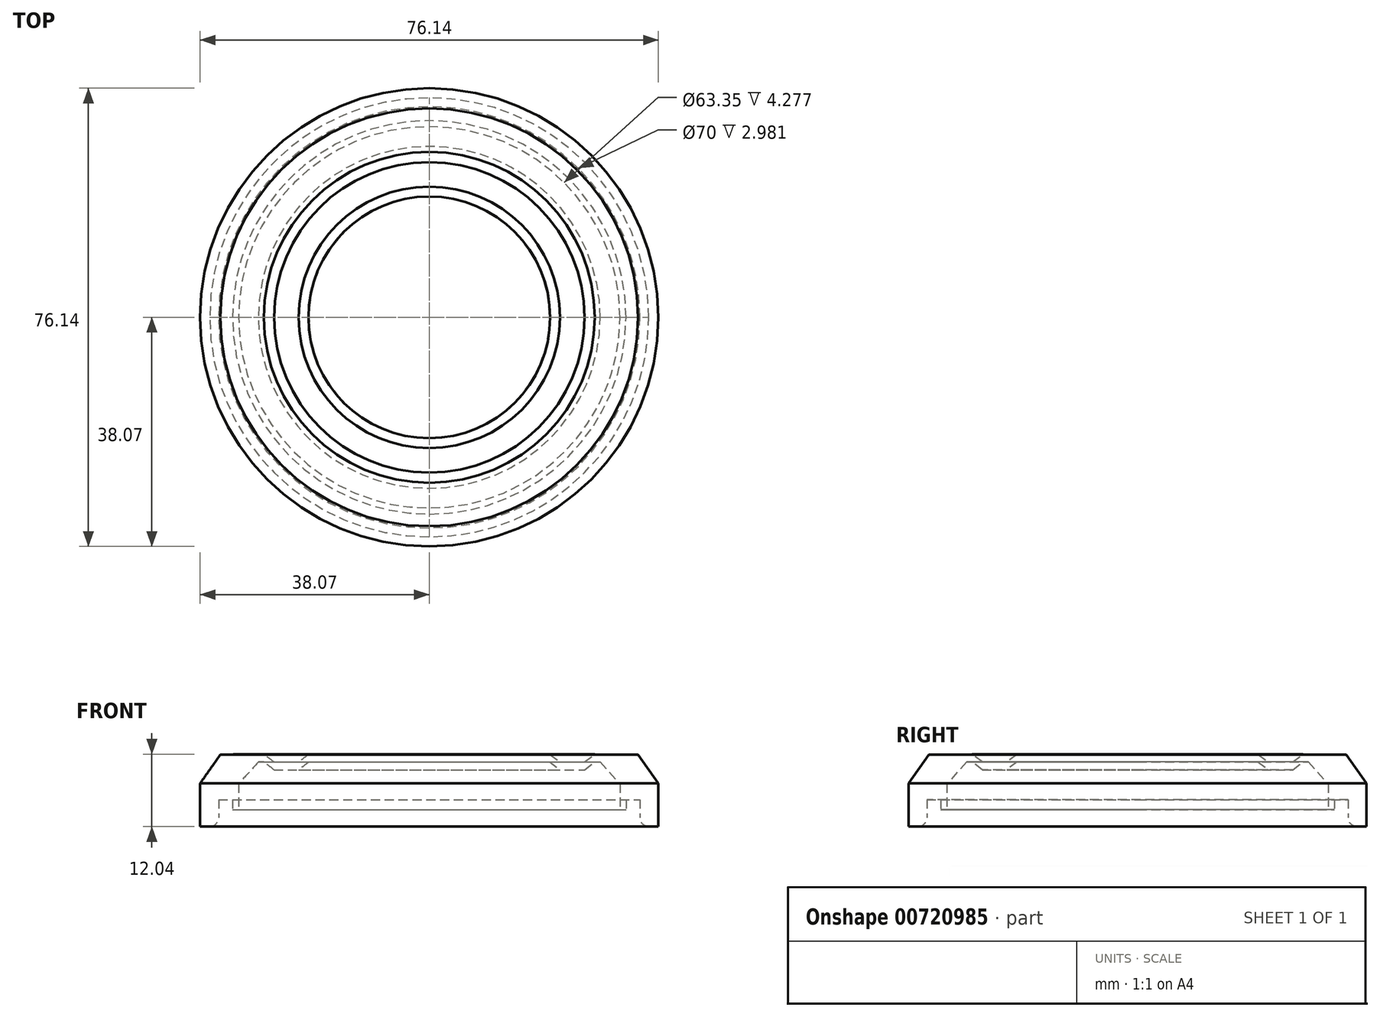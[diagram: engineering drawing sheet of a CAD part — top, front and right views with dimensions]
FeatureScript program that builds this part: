
annotation { "Feature Type Name" : "Feature", "Feature Type Description" : "" }
export const myFeature = defineFeature(function(context is Context, id is Id, definition is map)
    precondition{}
    {
        {
            var Q0;
            Q0=qCreatedBy(makeId("Front.planeOp"),FACE);
            var sketch = newSketch(context, id + "F0", { "sketchPlane" : qUnion([Q0])});
            skLineSegment(sketch, "E0", {"start": v(0, 0) * mm, "end": v(0, 19.91) * mm});
            skPoint(sketch, "E1.visualSharp", {"position": v(31, 6) * mm});
            skPoint(sketch, "E2.visualSharp", {"position": v(38, 6) * mm});
            skPoint(sketch, "E3.visualSharp", {"position": v(39, 6.04) * mm});
            skPoint(sketch, "E4.visualSharp", {"position": v(44, 6.04) * mm});
            skPoint(sketch, "E5.visualSharp", {"position": v(44.9, 6.04) * mm});
            skPoint(sketch, "E6.visualSharp", {"position": v(49.9, 6.04) * mm});
            skPoint(sketch, "E7.visualSharp", {"position": v(49.9, 0.04) * mm});
            skPoint(sketch, "E8.visualSharp", {"position": v(38, 0) * mm});
            skPoint(sketch, "E9.visualSharp", {"position": v(39, 0.01) * mm});
            skPoint(sketch, "E10.visualSharp", {"position": v(44, 0.01) * mm});
            skPoint(sketch, "E11.visualSharp", {"position": v(44.9, 0.04) * mm});
            skLineSegment(sketch, "E12", {"start": v(35, 8.36) * mm, "end": v(35, 11) * mm});
            skLineSegment(sketch, "E13", {"start": v(33.01, 11.34) * mm, "end": v(35, 11.34) * mm});
            skLineSegment(sketch, "E14", {"start": v(35, 11.34) * mm, "end": v(35, 8.36) * mm});
            skLineSegment(sketch, "E15", {"start": v(36.47, 6.86) * mm, "end": v(38.07, 6.86) * mm});
            skLineSegment(sketch, "E16", {"start": v(38.07, 6.86) * mm, "end": v(38.07, 14.07) * mm});
            skLineSegment(sketch, "E17", {"start": v(38.07, 14.07) * mm, "end": v(34.7, 18.84) * mm});
            skLineSegment(sketch, "E18", {"start": v(0, 18.84) * mm, "end": v(0, 17.6) * mm});
            skLineSegment(sketch, "E19", {"start": v(0, 17.6) * mm, "end": v(20, 17.6) * mm});
            skLineSegment(sketch, "E20", {"start": v(32.32, 9.7) * mm, "end": v(32.69, 9.7) * mm});
            skPoint(sketch, "E21.orphan", {"position": v(33, 6) * mm});
            skLineSegment(sketch, "E22", {"start": v(33.01, 11.34) * mm, "end": v(32.69, 11.34) * mm});
            skLineSegment(sketch, "E23", {"start": v(32.69, 11.34) * mm, "end": v(32.69, 9.7) * mm});
            skLineSegment(sketch, "E24", {"start": v(32.69, 9.7) * mm, "end": v(31.67, 9.7) * mm});
            skLineSegment(sketch, "E25", {"start": v(31.67, 9.7) * mm, "end": v(31.67, 13.98) * mm});
            skLineSegment(sketch, "E26", {"start": v(31.67, 13.98) * mm, "end": v(28.4, 17.6) * mm});
            skPoint(sketch, "E27.start.orphan", {"position": v(32.32, 14.07) * mm});
            skPoint(sketch, "E28.start.orphan", {"position": v(33.01, 11.02) * mm});
            skPoint(sketch, "E29.orphan", {"position": v(33.01, 9.7) * mm});
            skPoint(sketch, "E30.endSnap0", {"position": v(17.35, 18.84) * mm});
            skLineSegment(sketch, "E31.trimOffspring", {"start": v(20.08, 18.84) * mm, "end": v(0, 18.84) * mm});
            skPoint(sketch, "E32.start.orphan", {"position": v(27.48, 17.6) * mm});
            skPoint(sketch, "E33.end.orphan", {"position": v(27.48, 18.9) * mm});
            skLineSegment(sketch, "E34", {"start": v(34.7, 18.84) * mm, "end": v(27.48, 18.9) * mm});
            skLineSegment(sketch, "E35", {"start": v(28.4, 17.6) * mm, "end": v(27.48, 17.6) * mm});
            skLineSegment(sketch, "E36", {"start": v(27.48, 18.9) * mm, "end": v(25.8, 17.6) * mm});
            skLineSegment(sketch, "E37", {"start": v(20.08, 18.84) * mm, "end": v(21.71, 17.6) * mm});
            skLineSegment(sketch, "E38", {"start": v(21.71, 17.6) * mm, "end": v(25.8, 17.6) * mm});
            skLineSegment(sketch, "E39", {"start": v(27.48, 17.6) * mm, "end": v(25.8, 16.3) * mm});
            skLineSegment(sketch, "E40", {"start": v(25.8, 16.3) * mm, "end": v(21.7, 16.3) * mm});
            skLineSegment(sketch, "E41", {"start": v(21.7, 16.3) * mm, "end": v(20, 17.6) * mm});
            skPoint(sketch, "E42.orphan", {"position": v(17.35, 17.6) * mm});
            skLineSegment(sketch, "E43", {"start": v(40.5, 0.01) * mm, "end": v(40.4, 0.01) * mm});
            skLineSegment(sketch, "E44", {"start": v(36.1, 6) * mm, "end": v(36.4, 6) * mm});
            skLineSegment(sketch, "E45", {"start": v(33, 6) * mm, "end": v(32.9, 6) * mm});
            skLineSegment(sketch, "E46", {"start": v(36.4, 6) * mm, "end": v(36.1, 6) * mm});
            skLineSegment(sketch, "E47", {"start": v(39, 4.13) * mm, "end": v(39, 1.43) * mm});
            skPoint(sketch, "E48.visualSharp", {"position": v(34.64, 11.02) * mm});
            skLineSegment(sketch, "E49.filletArc", {"start": v(33.01, 11.02) * mm, "end": v(33.01, 11.02) * mm});
            skArc(sketch, "E50", {"start": v(35, 8.37) * mm, "mid": v(35.45, 7.3) * mm, "end": v(36.53, 6.86) * mm});
            skPoint(sketch, "E51.orphan", {"position": v(35, 6.86) * mm});
            skArc(sketch, "E52", {"start": v(33.51, 11.02) * mm, "mid": v(33.48, 11.02) * mm, "end": v(33.45, 11.02) * mm});
            skPoint(sketch, "E53.orphan", {"position": v(34.64, 6) * mm});
            skPoint(sketch, "E54.start.orphan", {"position": v(31, 0) * mm});
            skSolve(sketch);
        }
        {
            var Q0;
            {var subQ3=sQuery(id+"F0.wireOp",EDGE,"E15");Q0=makeQuery(id+"F0.imprint","IMPRINT",FACE,{"disambiguationData":[TD([[makeQuery(id+"F0.imprint","IMPRINT",EDGE,{"derivedFrom":subQ3}),1.0]])]});}
            var Q1;
            Q1=sQuery(id+"F0.wireOp",EDGE,"E0");
            revolve(context, id + "F1", {"entities" : qUnion([Q0]), "axis" : qUnion([Q1]), "revolveType" : RevolveType.FULL, "surfaceOperationType" : NewSurfaceOperationType.NEW});
        }
    });
